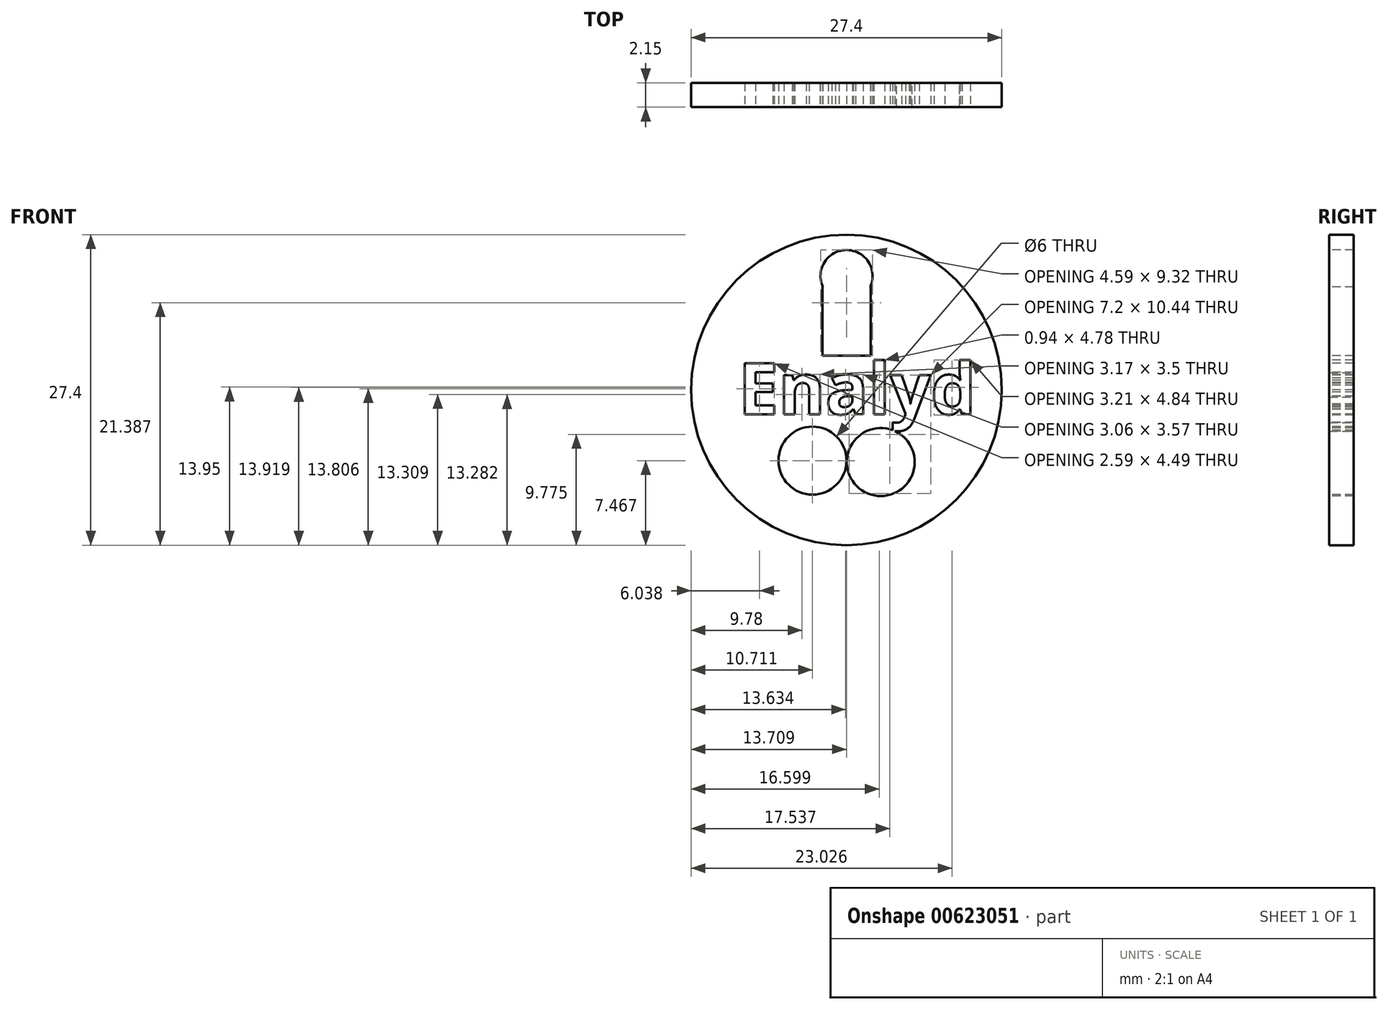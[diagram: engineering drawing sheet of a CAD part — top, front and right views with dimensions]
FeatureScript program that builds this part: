
annotation { "Feature Type Name" : "Feature", "Feature Type Description" : "" }
export const myFeature = defineFeature(function(context is Context, id is Id, definition is map)
    precondition{}
    {
        {
            var Q0;
            Q0=qCreatedBy(makeId("Front.planeOp"),FACE);
            var sketch = newSketch(context, id + "F0", { "sketchPlane" : qUnion([Q0])});
            skCircle(sketch, "E0", {"center": v(0, 0) * mm, "radius": 13.7 * mm});
            skSolve(sketch);
        }
        {
            var Q0;
            Q0=sQuery(id+"F0.wireOp",EDGE,"E0");
            extrude(context, id + "F1", {"bodyType" : ToolBodyType.SURFACE, "surfaceEntities" : qUnion([Q0]), "depth" : 2.15 * mm, "offsetDistance" : 25 * mm});
        }
        {
            var Q0;
            Q0 = qSketchRegion(id + "F0", true);
            extrude(context, id + "F2", {"entities" : qUnion([Q0]), "depth" : 2.15 * mm, "offsetDistance" : 25 * mm});
        }
        {
            var Q0;
            Q0=makeQuery(id+"F2.opExtrude","CAP_FACE",FACE,{"disambiguationData":[OSD([sQuery(id+"F0.wireOp",EDGE,"E0")])],"isStart":false});
            var sketch = newSketch(context, id + "F3", { "sketchPlane" : qUnion([Q0])});
            skText(sketch, "E1", { "text": "Enalyd", "fontName": "OpenSans-Bold.ttf"});
            const initialGuessF3  = {"E1": [-0.00952, -0.00214, 1, 0, 0.00453]};
            skSetInitialGuess(sketch, initialGuessF3);
            skSolve(sketch);
        }
        {
            var Q0;
            Q0 = qSketchRegion(id + "F3", true);
            extrude(context, id + "F4", {"entities" : qUnion([Q0]), "operationType" : NewBodyOperationType.REMOVE, "oppositeDirection" : true, "depth" : 15 * mm, "offsetDistance" : 25 * mm});
        }
        {
            var Q0;
            Q0=makeQuery(id+"F3.imprint","IMPRINT",FACE,{"disambiguationData":[TD([[makeQuery(id+"F3.imprint","IMPRINT",EDGE,{"derivedFrom":sQuery(id+"F3.wireOp",EDGE,"E1.sketch_text.stroke-0")}),1.0]])]});
            var sketch = newSketch(context, id + "F5", { "sketchPlane" : qUnion([Q0])});
            skCircle(sketch, "E2", {"center": v(-2.99, -6.23) * mm, "radius": 3 * mm});
            skSolve(sketch);
        }
        {
            var Q0;
            Q0 = qSketchRegion(id + "F5", true);
            extrude(context, id + "F6", {"entities" : qUnion([Q0]), "operationType" : NewBodyOperationType.REMOVE, "endBound" : BoundingType.UP_TO_NEXT, "oppositeDirection" : true, "depth" : 25 * mm, "offsetDistance" : 25 * mm});
        }
        {
            var Q0;
            Q0=makeQuery(id+"F3.imprint","IMPRINT",FACE,{"disambiguationData":[TD([[makeQuery(id+"F3.imprint","IMPRINT",EDGE,{"derivedFrom":sQuery(id+"F3.wireOp",EDGE,"E1.sketch_text.stroke-0")}),1.0]])]});
            var sketch = newSketch(context, id + "F7", { "sketchPlane" : qUnion([Q0])});
            skCircle(sketch, "E3", {"center": v(3.03, -6.36) * mm, "radius": 3 * mm});
            skSolve(sketch);
        }
        {
            var Q0;
            Q0=makeQuery(id+"F7.imprint","IMPRINT",FACE,{"disambiguationData":[TD([[makeQuery(id+"F7.imprint","IMPRINT",EDGE,{"derivedFrom":sQuery(id+"F7.wireOp",EDGE,"E3")}),1.0]])]});
            extrude(context, id + "F8", {"entities" : qUnion([Q0]), "operationType" : NewBodyOperationType.REMOVE, "endBound" : BoundingType.UP_TO_NEXT, "oppositeDirection" : true, "depth" : 25 * mm, "offsetDistance" : 25 * mm});
        }
        {
            var Q0;
            Q0=makeQuery(id+"F3.imprint","IMPRINT",FACE,{"disambiguationData":[TD([[makeQuery(id+"F3.imprint","IMPRINT",EDGE,{"derivedFrom":sQuery(id+"F3.wireOp",EDGE,"E1.sketch_text.stroke-0")}),1.0]])]});
            var sketch = newSketch(context, id + "F9", { "sketchPlane" : qUnion([Q0])});
            skLineSegment(sketch, "E4.bottom", {"start": v(-2.12, 9.08) * mm, "end": v(2.15, 9.08) * mm});
            skLineSegment(sketch, "E4.top", {"start": v(-2.12, 3.03) * mm, "end": v(2.15, 3.03) * mm});
            skLineSegment(sketch, "E4.left", {"start": v(-2.12, 9.08) * mm, "end": v(-2.12, 3.03) * mm});
            skLineSegment(sketch, "E4.right", {"start": v(2.15, 9.08) * mm, "end": v(2.15, 3.03) * mm});
            skSolve(sketch);
        }
        {
            var Q0;
            Q0=makeQuery(id+"F9.imprint","IMPRINT",FACE,{"disambiguationData":[TD([[makeQuery(id+"F9.imprint","IMPRINT",EDGE,{"derivedFrom":sQuery(id+"F9.wireOp",EDGE,"E4.bottom")}),-1.0]])]});
            extrude(context, id + "F10", {"entities" : qUnion([Q0]), "operationType" : NewBodyOperationType.REMOVE, "endBound" : BoundingType.UP_TO_NEXT, "oppositeDirection" : true, "depth" : 25 * mm, "offsetDistance" : 25 * mm});
        }
        {
            var Q0;
            Q0=makeQuery(id+"F3.imprint","IMPRINT",FACE,{"disambiguationData":[TD([[makeQuery(id+"F3.imprint","IMPRINT",EDGE,{"derivedFrom":sQuery(id+"F3.wireOp",EDGE,"E1.sketch_text.stroke-0")}),1.0]])]});
            var sketch = newSketch(context, id + "F11", { "sketchPlane" : qUnion([Q0])});
            skCircle(sketch, "E5", {"center": v(0, 10.05) * mm, "radius": 2.3 * mm});
            skPoint(sketch, "E5.first.point", {"position": v(2.17, 9.24) * mm});
            skPoint(sketch, "E5.second.point", {"position": v(-2.24, 10.52) * mm});
            skPoint(sketch, "E5.third.point", {"position": v(-0.16, 12.34) * mm});
            skSolve(sketch);
        }
        {
            var Q0;
            Q0 = qSketchRegion(id + "F11", true);
            extrude(context, id + "F12", {"entities" : qUnion([Q0]), "operationType" : NewBodyOperationType.REMOVE, "endBound" : BoundingType.UP_TO_NEXT, "oppositeDirection" : true, "depth" : 25 * mm, "offsetDistance" : 25 * mm});
        }
    });
